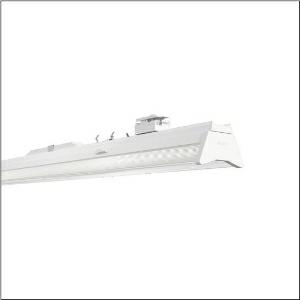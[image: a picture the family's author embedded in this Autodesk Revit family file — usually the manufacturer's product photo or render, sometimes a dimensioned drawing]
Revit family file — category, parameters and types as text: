
# Revit family: licross_11_performance_mo_51tm167n485g
name_source: partatom
category: Lighting Fixtures
units: mm (PartAtom-declared; Revit-internal decimal feet)

## family parameters
Cut with Voids When Loaded = No
Host = Face
Light Source = No
Part Type = Normal
Room Calculation Point = No
Round Connector Dimension = Use Diameter
Shared = No

## types (1)
- Licross 11 Performance MO (1 x LED, 8840 lm, 48.6 W, 4000K)
    Apparent Load = 49 VA
    CIE Flux Codes = 66 88 96 79 100
    Color Rendering = 80
    Color Temperature = 4000K
    Default Elevation = 1800 mm
    Description = Licross 11 Performance MO, luminaire insert, of sheet steel, galvanised, coil coated, white, length: 1.500mm, width: 120mm, height: 123mm, LED rated luminous flux: 8.840lm, light colour: 840, SDCM (Standard Deviation of Colour Matching)MacAdam ≤ 2 SDCM (initial), control gear: ON/OFF, with plug, 3-pole, with phase selection, mains connection: 220..240V, AC, 50/60Hz, rated input power: 49W, internal wiring halogen-free, primary light control with lens, of plastic, primary optical cover: cover, of PMMA, light emission: direct/indirect distribution, primary light characteristic: symmetric, protection rating (complete): IP40, insulation class (complete): insulation class I (protective earthing), certification: CE, ENEC, VDE, UKCA, protection symbol: D if used in an environment without relevant dust loads with corresponding accessories, impact resistance: IK06, permissible ambient temperature for indoor applications: -25..+35°C, corresponds to IFS (International Featured Standards) requirements for safety and quality in the food industry, reducing of maximum allowable ambient temperature of 5°C with ceiling mounting, LABS conformity tested according to VDMA 24364:2018-05, The light source and the operating device comply with the requirements of the Ecodesign Regulation (EU) 2019/2020 and are replaceable in accordance with this regulation, packaging unit: 1 piece
    Height = 114 mm
    Lamp = 1 x LED
    Lamp Light Flux = 8840 lm
    Lamp Power = 48.6 W
    Lamp count = 1
    Length = 1500 mm
    Luminous efficacy = 182 lm/W
    Manufacturer = Siteco
    ModVariant = No
    Model = 51TM167N485G
    Mounting Place = Ceiling
    Mounting Type = Pendant
    Number of Poles = 1
    OnlyDefault = Yes
    Power Factor = 1
    Product Name = Licross 11 Performance MO
    Product group = luminaire insert | ceiling pendant
    ProductGroupID = 901
    Protection Class = Protection class I
    Protection Degree = IP 40
    RLX_Detail_Level = 1
    RLX_Emergency_Light_Flux = 0 lm
    RLX_Emergency_Type = 0
    RLX_Emergency_Type_DB = No
    RlxData = <blob elided: 30641 chars, md5=2a45868a>
    Socket = socket
    Standby Power = 0 W
    System Light Flux = 8840 lm
    System Power = 49 W
    Type Comments = Product without accessories
    Type Image = l_1256138.jpg
    URL = http://relux.com
    VarID = ---
    Voltage = 0 V
    Weight = 0.00 kg
    Width = 120 mm

## geometry (parser evidence)
native form markers: Blend x4, Sweep x12
no freeform markers — native parametric forms only
